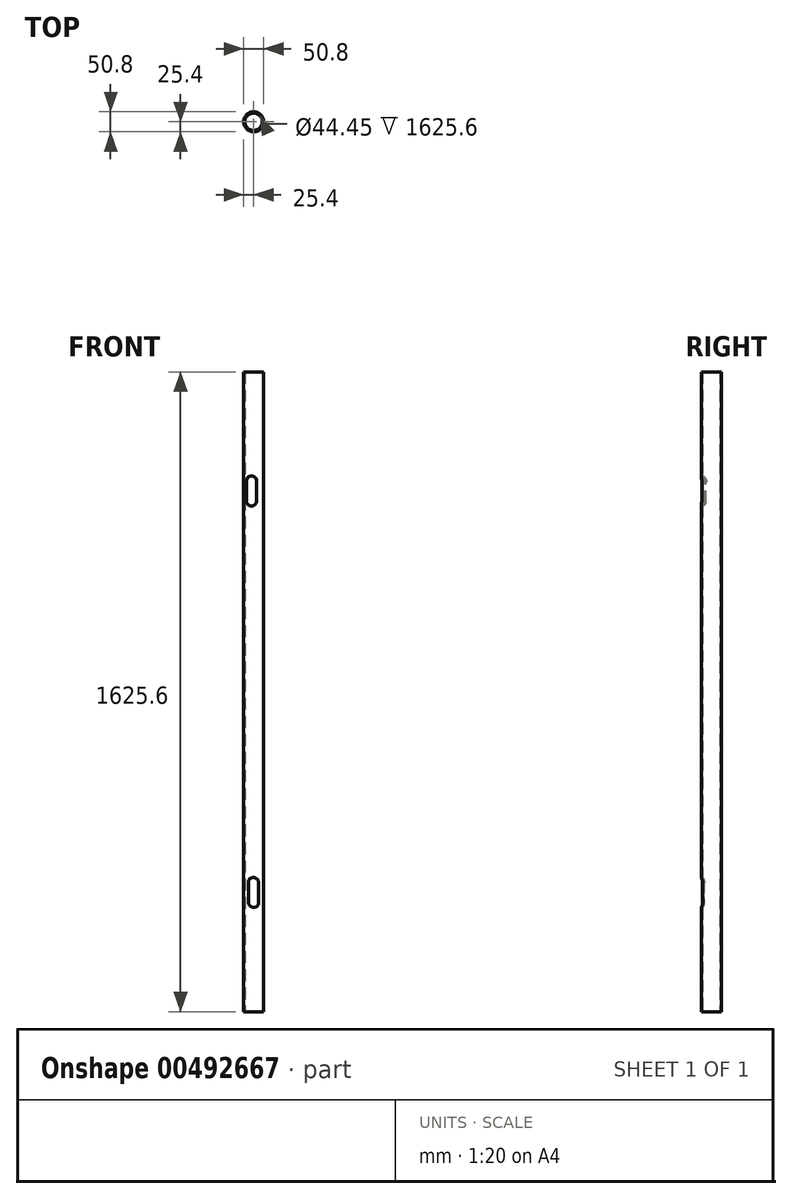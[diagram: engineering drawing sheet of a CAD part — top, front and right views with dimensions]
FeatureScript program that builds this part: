
annotation { "Feature Type Name" : "Feature", "Feature Type Description" : "" }
export const myFeature = defineFeature(function(context is Context, id is Id, definition is map)
    precondition{}
    {
        {
            assignVariable(context, id + "F0", {"name" : "hmi_height", "anyValue" : 1625.6 * mm});
        }
        {
            var Q0;
            Q0=qCreatedBy(makeId("Top.planeOp"),FACE);
            var sketch = newSketch(context, id + "F1", { "sketchPlane" : qUnion([Q0])});
            skCircle(sketch, "E0", {"center": v(0, 0) * mm, "radius": 25.4 * mm});
            skCircle(sketch, "E1", {"center": v(0, 0) * mm, "radius": 22.22 * mm});
            skSolve(sketch);
        }
        {
            var Q0;
            Q0 = qSketchRegion(id + "F1", true);
            extrude(context, id + "F2", {"entities" : qUnion([Q0]), "depth" : getVariable(context, 'hmi_height')});
        }
        {
            var Q0;
            Q0=qCreatedBy(makeId("Front.planeOp"),FACE);
            var sketch = newSketch(context, id + "F3", { "sketchPlane" : qUnion([Q0])});
            skLineSegment(sketch, "E2", {"start": v(0, 0) * mm, "end": v(0, 1625.6) * mm, "construction": true});
            skLineSegment(sketch, "E3", {"start": v(-16.53, 812.8) * mm, "end": v(-16.53, 812.8) * mm});
            skPoint(sketch, "E3.startSnap0", {"position": v(0, 812.8) * mm});
            skPoint(sketch, "E3.endSnap0", {"position": v(0, 812.8) * mm});
            skPoint(sketch, "E4.middle", {"position": v(0, 304.8) * mm});
            skLineSegment(sketch, "E5", {"start": v(-13.09, 331.7) * mm, "end": v(-12.37, 281.53) * mm});
            skLineSegment(sketch, "E6", {"start": v(13.09, 277.9) * mm, "end": v(12.37, 328.07) * mm});
            skArc(sketch, "E7", {"start": v(12.37, 328.07) * mm, "mid": v(1.19, 340.76) * mm, "end": v(-13.09, 331.7) * mm});
            skArc(sketch, "E8", {"start": v(-12.37, 281.53) * mm, "mid": v(-1.76, 264.83) * mm, "end": v(13.09, 277.9) * mm});
            skArc(sketch, "E9.MirrorCS", {"start": v(7.56, 1297.8) * mm, "mid": v(-3.5, 1284.99) * mm, "end": v(-17.86, 1293.91) * mm});
            skLineSegment(sketch, "E10.MirrorCS", {"start": v(-17.86, 1293.91) * mm, "end": v(-17.63, 1344.08) * mm});
            skLineSegment(sketch, "E11.MirrorCS", {"start": v(7.78, 1347.97) * mm, "end": v(7.56, 1297.8) * mm});
            skArc(sketch, "E12.MirrorCS", {"start": v(-17.63, 1344.08) * mm, "mid": v(-7.2, 1360.89) * mm, "end": v(7.78, 1347.97) * mm});
            skSolve(sketch);
        }
        {
            var Q0;
            Q0 = qSketchRegion(id + "F3", true);
            extrude(context, id + "F4", {"entities" : qUnion([Q0]), "operationType" : NewBodyOperationType.REMOVE, "depth" : 50 * mm, "offsetDistance" : 25 * mm});
        }
    });
